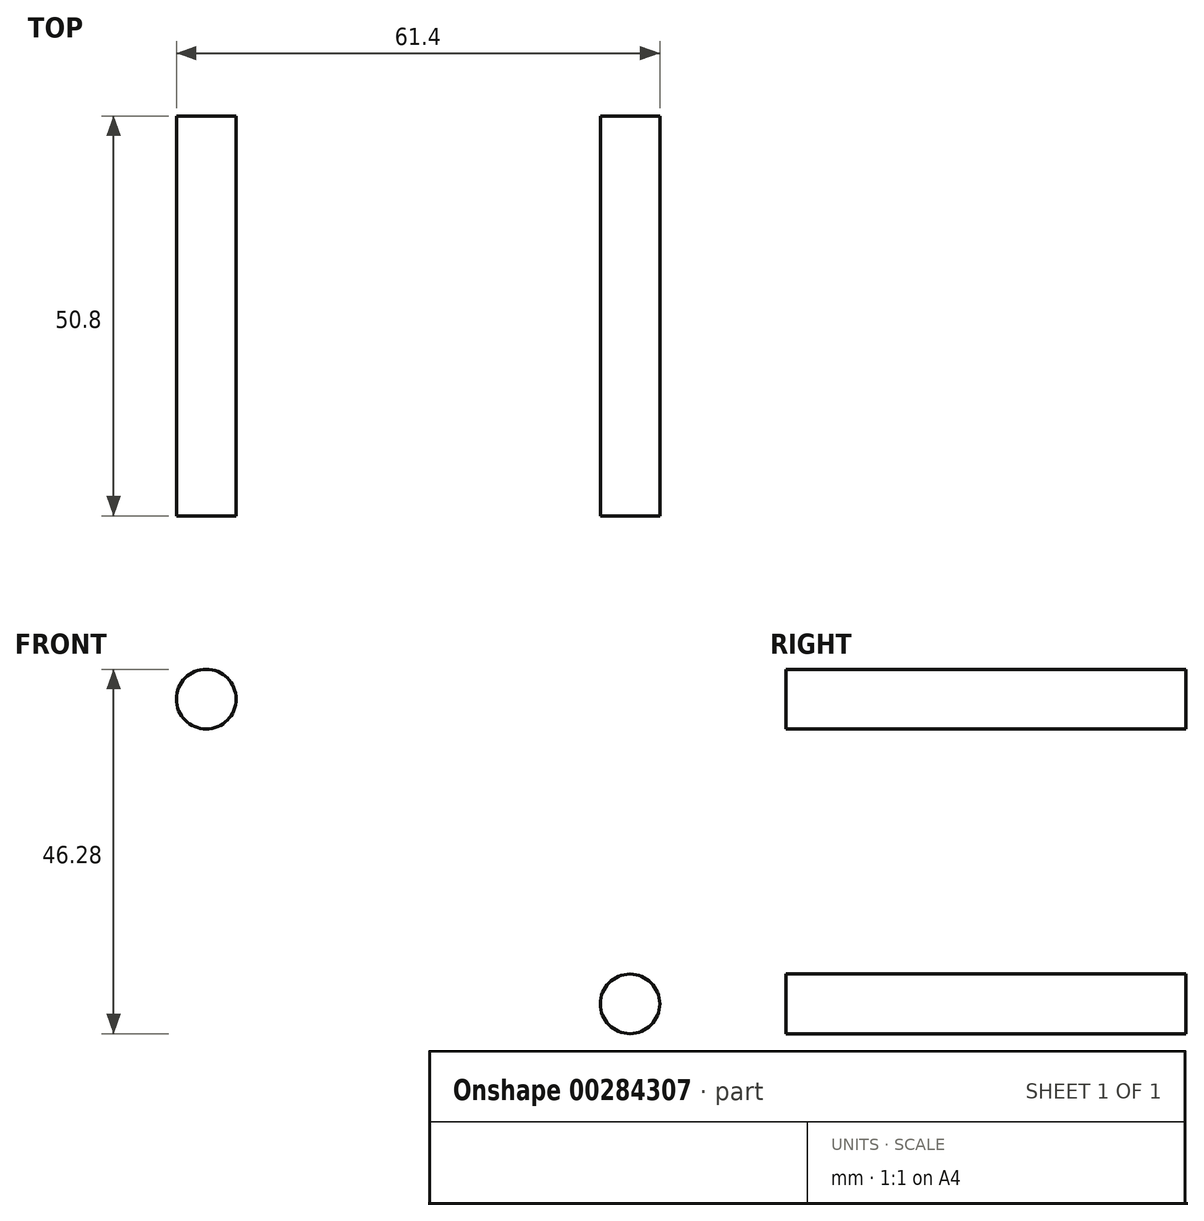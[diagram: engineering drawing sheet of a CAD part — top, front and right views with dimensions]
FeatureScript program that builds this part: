
annotation { "Feature Type Name" : "Feature", "Feature Type Description" : "" }
export const myFeature = defineFeature(function(context is Context, id is Id, definition is map)
    precondition{}
    {
        {
            var Q0;
            Q0=qCreatedBy(makeId("Front.planeOp"),FACE);
            var sketch = newSketch(context, id + "F0", { "sketchPlane" : qUnion([Q0])});
            skCircle(sketch, "E0", {"center": v(-26.92, 19.36) * mm, "radius": 3.78 * mm});
            skCircle(sketch, "E1.MirrorC", {"center": v(26.92, 19.36) * mm, "radius": 3.78 * mm});
            skCircle(sketch, "E2.MirrorC", {"center": v(26.92, -19.36) * mm, "radius": 3.78 * mm});
            skCircle(sketch, "E3.MirrorC", {"center": v(-26.92, -19.36) * mm, "radius": 3.78 * mm});
            skSolve(sketch);
        }
        {
            var Q0;
            Q0=makeQuery(id+"F0.imprint","IMPRINT",FACE,{"disambiguationData":[TD([[makeQuery(id+"F0.imprint","IMPRINT",EDGE,{"derivedFrom":sQuery(id+"F0.wireOp",EDGE,"E0")}),1.0]])]});
            var Q1;
            Q1=makeQuery(id+"F0.imprint","IMPRINT",FACE,{"disambiguationData":[TD([[makeQuery(id+"F0.imprint","IMPRINT",EDGE,{"derivedFrom":sQuery(id+"F0.wireOp",EDGE,"E1.MirrorC")}),-1.0]])]});
            var Q2;
            Q2=makeQuery(id+"F0.imprint","IMPRINT",FACE,{"disambiguationData":[TD([[makeQuery(id+"F0.imprint","IMPRINT",EDGE,{"derivedFrom":sQuery(id+"F0.wireOp",EDGE,"E2.MirrorC")}),1.0]])]});
            var Q3;
            Q3=makeQuery(id+"F0.imprint","IMPRINT",FACE,{"disambiguationData":[TD([[makeQuery(id+"F0.imprint","IMPRINT",EDGE,{"derivedFrom":sQuery(id+"F0.wireOp",EDGE,"E3.MirrorC")}),-1.0]])]});
            extrude(context, id + "F1", {"entities" : qUnion([Q0, Q1, Q2, Q3]), "depth" : 50.8 * mm});
        }
    });
